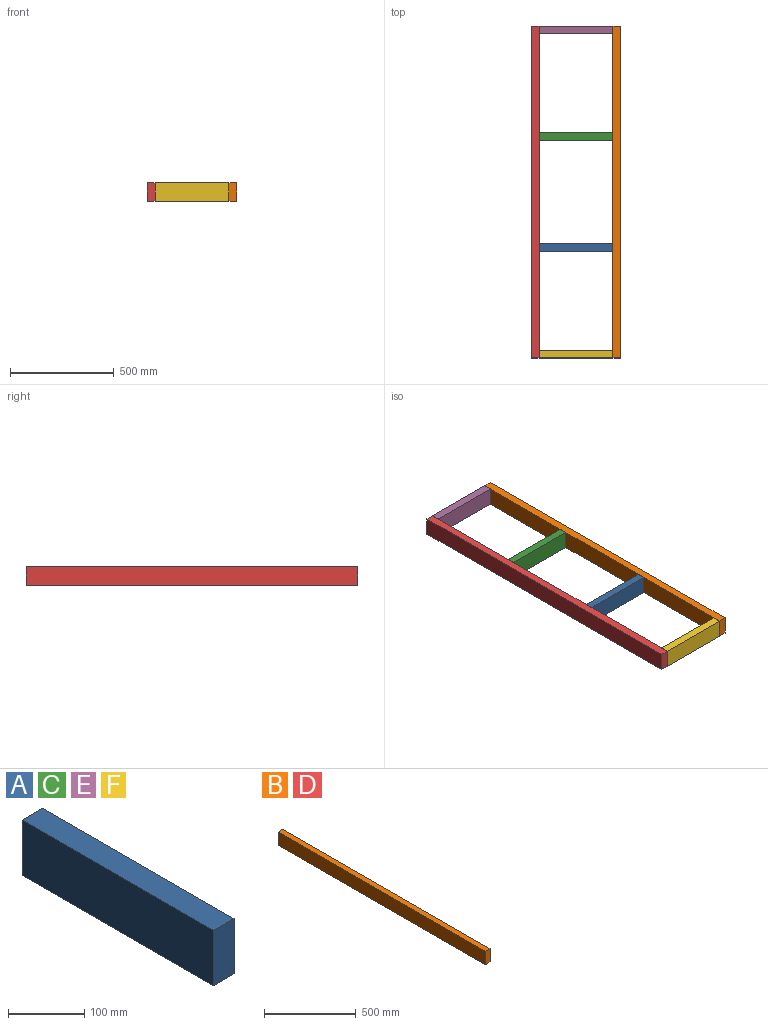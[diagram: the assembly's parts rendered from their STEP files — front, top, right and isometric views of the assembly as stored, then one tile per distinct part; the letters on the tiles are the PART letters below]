
ASSEMBLY  parts=6 mates=5
PART A: 6 faces, bbox 38.1x355.6x88.9 mm
  f0: plane 355.6x88.9mm, normal (-1,0,0), area 31612.8mm2, adj f1,f3,f4,f5
  f1: plane 355.6x38.1mm, normal (0,0,-1), area 13548.4mm2, adj f0,f2,f4,f5
  f2: plane 355.6x88.9mm, normal (1,0,0), area 31612.8mm2, adj f1,f3,f4,f5
  f3: plane 355.6x38.1mm, normal (0,0,1), area 13548.4mm2, adj f0,f2,f4,f5
  f4: plane 88.9x38.1mm, normal (0,-1,0), area 3387.1mm2, adj f0,f1,f2,f3
  f5: plane 88.9x38.1mm, normal (0,1,0), area 3387.1mm2, adj f0,f1,f2,f3
PART B: 6 faces, bbox 38.1x1600.2x88.9 mm
  f0: plane 1600.2x88.9mm, normal (-1,0,0), area 142257.8mm2, adj f1,f3,f4,f5
  f1: plane 1600.2x38.1mm, normal (0,0,-1), area 60967.6mm2, adj f0,f2,f4,f5
  f2: plane 1600.2x88.9mm, normal (1,0,0), area 142257.8mm2, adj f1,f3,f4,f5
  f3: plane 1600.2x38.1mm, normal (0,0,1), area 60967.6mm2, adj f0,f2,f4,f5
  f4: plane 88.9x38.1mm, normal (0,-1,0), area 3387.1mm2, adj f0,f1,f2,f3
  f5: plane 88.9x38.1mm, normal (0,1,0), area 3387.1mm2, adj f0,f1,f2,f3
PART C: same geometry as A
PART D: same geometry as B
PART E: same geometry as A
PART F: same geometry as A
PLACE A rot(axis=(0.71,0.71,0),180deg) t=(-126.38,-735.89,-196.86)mm
PLACE B t=(-126.38,349.96,-285.76)mm
PLACE C rot(axis=(0.71,0.71,0),180deg) t=(-126.38,-202.49,-196.86)mm
PLACE D t=(-520.08,349.96,-285.76)mm
PLACE E rot(axis=(0,0,1),90deg) t=(-481.98,311.86,-285.76)mm
PLACE F rot(axis=(0,0,-1),90deg) t=(-126.38,-1212.14,-285.76)mm
MATE fastened C.f4 <-> D.f2  axis (-1,0,0) through (-481.98,-183.44,-241.31)mm
MATE fastened B.f0 <-> F.f5  axis (-1,0,0) through (-126.38,-1250.24,-241.31)mm
MATE fastened F.f4 <-> D.f2  axis (-1,0,0) through (-481.98,-1250.24,-241.31)mm
MATE fastened E.f4 <-> B.f0  axis (1,0,0) through (-126.38,349.96,-241.31)mm
MATE fastened A.f4 <-> D.f2  axis (-1,0,0) through (-481.98,-716.84,-241.31)mm
